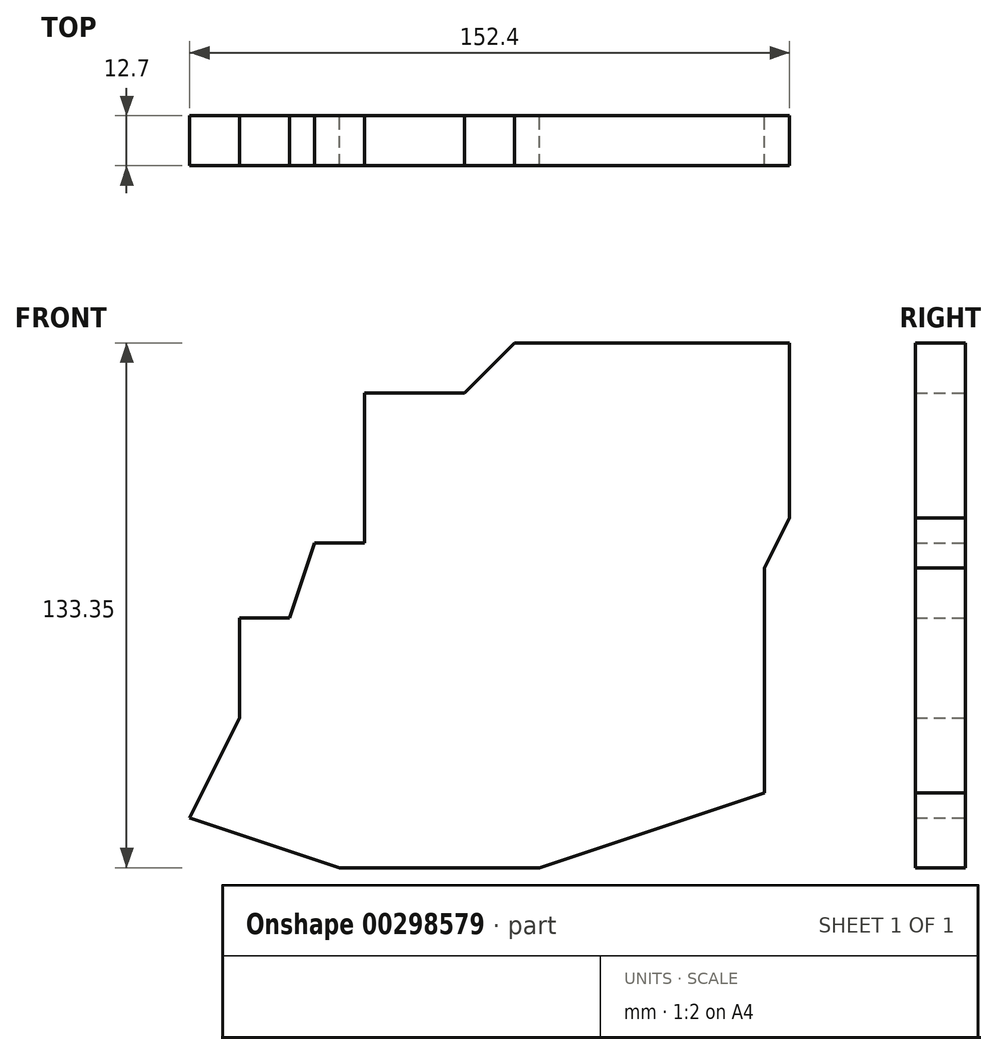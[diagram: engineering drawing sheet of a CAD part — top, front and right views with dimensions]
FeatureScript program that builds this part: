
annotation { "Feature Type Name" : "Feature", "Feature Type Description" : "" }
export const myFeature = defineFeature(function(context is Context, id is Id, definition is map)
    precondition{}
    {
        {
            var Q0;
            Q0=qCreatedBy(makeId("Front.planeOp"),FACE);
            var sketch = newSketch(context, id + "F0", { "sketchPlane" : qUnion([Q0])});
            skPoint(sketch, "E0", {"position": v(-99.52, -54.64) * mm});
            skPoint(sketch, "E1", {"position": v(-61.42, -67.34) * mm});
            skPoint(sketch, "E2", {"position": v(-10.62, -67.34) * mm});
            skPoint(sketch, "E3", {"position": v(46.53, -48.29) * mm});
            skPoint(sketch, "E4", {"position": v(46.53, 8.86) * mm});
            skPoint(sketch, "E5", {"position": v(52.88, 21.56) * mm});
            skPoint(sketch, "E6", {"position": v(52.88, 66.01) * mm});
            skPoint(sketch, "E7", {"position": v(-16.97, 66.01) * mm});
            skPoint(sketch, "E8", {"position": v(-29.67, 53.31) * mm});
            skPoint(sketch, "E9", {"position": v(-55.07, 53.31) * mm});
            skPoint(sketch, "E10", {"position": v(-55.07, 15.21) * mm});
            skPoint(sketch, "E11", {"position": v(-67.77, 15.21) * mm});
            skPoint(sketch, "E12", {"position": v(-74.12, -3.84) * mm});
            skPoint(sketch, "E13", {"position": v(-86.82, -3.84) * mm});
            skPoint(sketch, "E14", {"position": v(-86.82, -29.24) * mm});
            skLineSegment(sketch, "E15", {"start": v(-99.52, -54.64) * mm, "end": v(-61.42, -67.34) * mm});
            skLineSegment(sketch, "E16", {"start": v(-61.42, -67.34) * mm, "end": v(-10.62, -67.34) * mm});
            skLineSegment(sketch, "E17", {"start": v(-10.62, -67.34) * mm, "end": v(46.53, -48.29) * mm});
            skLineSegment(sketch, "E18", {"start": v(46.53, -48.29) * mm, "end": v(46.53, 8.86) * mm});
            skLineSegment(sketch, "E19", {"start": v(46.53, 8.86) * mm, "end": v(52.88, 21.56) * mm});
            skLineSegment(sketch, "E20", {"start": v(52.88, 21.56) * mm, "end": v(52.88, 66.01) * mm});
            skLineSegment(sketch, "E21", {"start": v(52.88, 66.01) * mm, "end": v(-16.97, 66.01) * mm});
            skLineSegment(sketch, "E22", {"start": v(-29.67, 53.31) * mm, "end": v(-16.97, 66.01) * mm});
            skLineSegment(sketch, "E23", {"start": v(-29.67, 53.31) * mm, "end": v(-55.07, 53.31) * mm});
            skLineSegment(sketch, "E24", {"start": v(-55.07, 53.31) * mm, "end": v(-55.07, 15.21) * mm});
            skLineSegment(sketch, "E25", {"start": v(-67.77, 15.21) * mm, "end": v(-55.07, 15.21) * mm});
            skLineSegment(sketch, "E26", {"start": v(-67.77, 15.21) * mm, "end": v(-74.12, -3.84) * mm});
            skLineSegment(sketch, "E27", {"start": v(-86.82, -3.84) * mm, "end": v(-86.82, -29.24) * mm});
            skLineSegment(sketch, "E28", {"start": v(-86.82, -29.24) * mm, "end": v(-99.52, -54.64) * mm});
            skLineSegment(sketch, "E29", {"start": v(-86.82, -3.84) * mm, "end": v(-74.12, -3.84) * mm});
            skSolve(sketch);
        }
        {
            var Q0;
            Q0=makeQuery(id+"F0.imprint","IMPRINT",FACE,{"disambiguationData":[TD([[makeQuery(id+"F0.imprint","IMPRINT",EDGE,{"derivedFrom":sQuery(id+"F0.wireOp",EDGE,"E15")}),1.0]])]});
            extrude(context, id + "F1", {"entities" : qUnion([Q0]), "depth" : 12.7 * mm});
        }
    });
